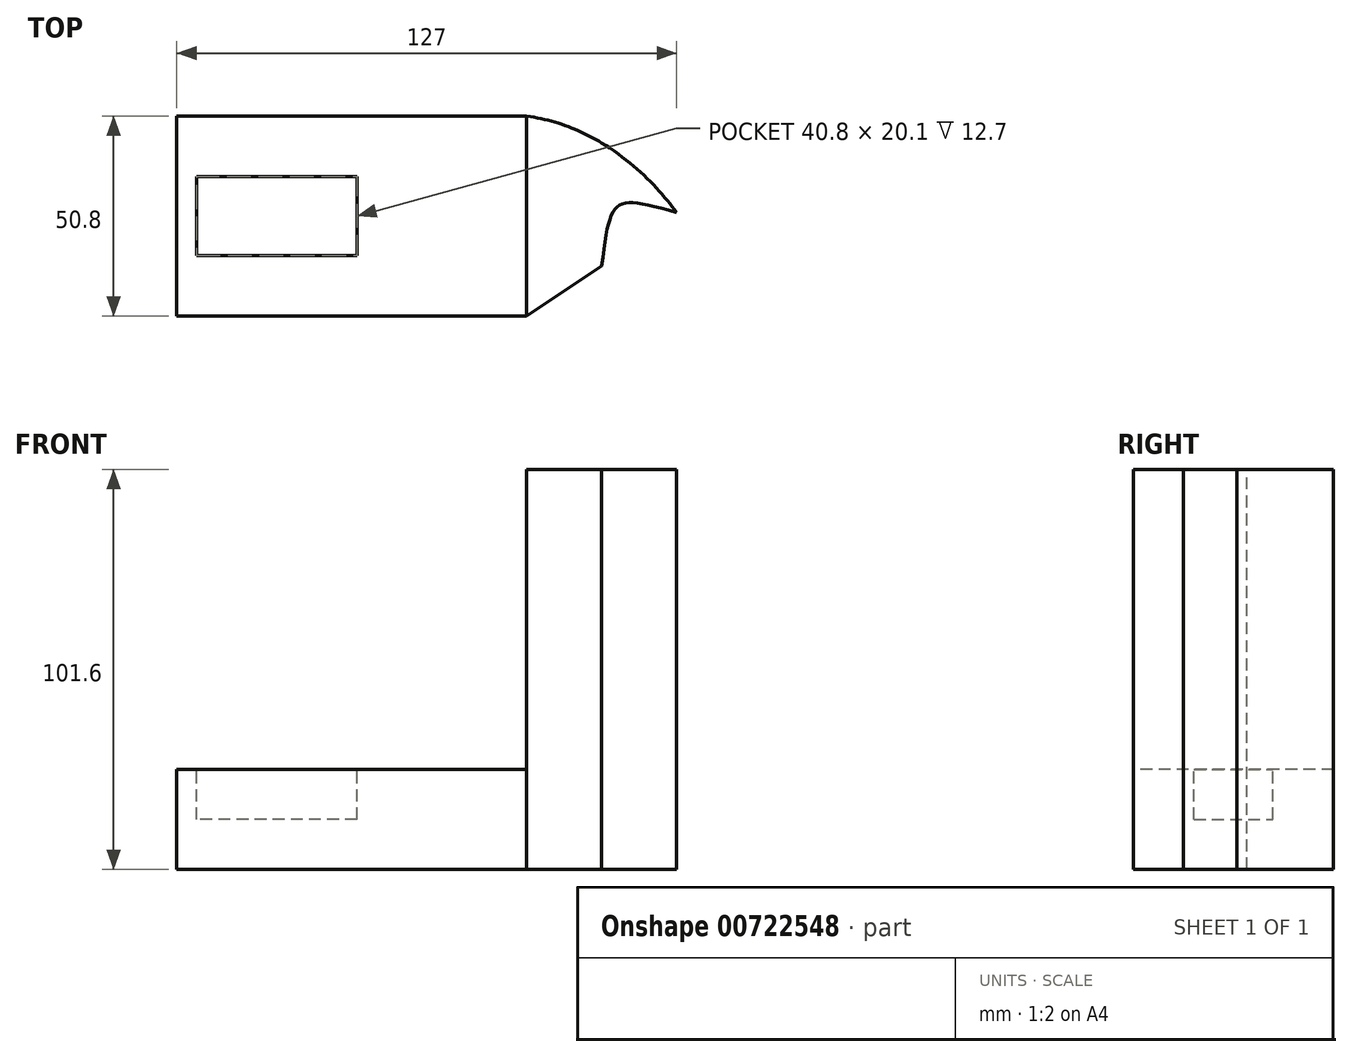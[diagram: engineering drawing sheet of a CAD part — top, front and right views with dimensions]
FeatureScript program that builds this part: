
annotation { "Feature Type Name" : "Feature", "Feature Type Description" : "" }
export const myFeature = defineFeature(function(context is Context, id is Id, definition is map)
    precondition{}
    {
        {
            var Q0;
            Q0=qCreatedBy(makeId("Top.planeOp"),FACE);
            var sketch = newSketch(context, id + "F0", { "sketchPlane" : qUnion([Q0])});
            skLineSegment(sketch, "E0.bottom", {"start": v(50.8, -25.4) * mm, "end": v(-50.8, -25.4) * mm});
            skLineSegment(sketch, "E0.top", {"start": v(50.8, 25.4) * mm, "end": v(-50.8, 25.4) * mm});
            skLineSegment(sketch, "E0.left", {"start": v(50.8, -25.4) * mm, "end": v(50.8, 25.4) * mm});
            skLineSegment(sketch, "E0.right", {"start": v(-50.8, -25.4) * mm, "end": v(-50.8, 25.4) * mm});
            skPoint(sketch, "E0.middle", {"position": v(0, 0) * mm});
            skSolve(sketch);
        }
        {
            var Q0;
            Q0=makeQuery(id+"F0.imprint","IMPRINT",FACE,{"disambiguationData":[TD([[makeQuery(id+"F0.imprint","IMPRINT",EDGE,{"derivedFrom":sQuery(id+"F0.wireOp",EDGE,"E0.bottom")}),-1.0]])]});
            extrude(context, id + "F1", {"entities" : qUnion([Q0]), "depth" : 25.4 * mm, "offsetDistance" : 25.4 * mm});
        }
        {
            var Q0;
            Q0=makeQuery(id+"F1.opExtrude","CAP_FACE",FACE,{"disambiguationData":[OSD([sQuery(id+"F0.wireOp",EDGE,"E0.bottom"),sQuery(id+"F0.wireOp",EDGE,"E0.top"),sQuery(id+"F0.wireOp",EDGE,"E0.left"),sQuery(id+"F0.wireOp",EDGE,"E0.right")])],"isStart":false});
            var sketch = newSketch(context, id + "F2", { "sketchPlane" : qUnion([Q0])});
            skLineSegment(sketch, "E1", {"start": v(-50.8, 25.4) * mm, "end": v(0, -25.4) * mm});
            skLineSegment(sketch, "E2", {"start": v(0, -25.4) * mm, "end": v(0, 25.4) * mm});
            skLineSegment(sketch, "E3", {"start": v(0, 25.4) * mm, "end": v(-50.8, -25.4) * mm});
            skCircle(sketch, "E4", {"center": v(-25.4, 0) * mm, "radius": 14.63 * mm});
            skCircle(sketch, "E5", {"center": v(-25.4, 0) * mm, "radius": 3.81 * mm});
            skLineSegment(sketch, "E6.bottom", {"start": v(-5, -10.05) * mm, "end": v(-45.8, -10.05) * mm});
            skLineSegment(sketch, "E6.top", {"start": v(-5, 10.05) * mm, "end": v(-45.8, 10.05) * mm});
            skLineSegment(sketch, "E6.left", {"start": v(-5, -10.05) * mm, "end": v(-5, 10.05) * mm});
            skLineSegment(sketch, "E6.right", {"start": v(-45.8, -10.05) * mm, "end": v(-45.8, 10.05) * mm});
            skSolve(sketch);
        }
        {
            var Q0;
            {var subQ0=sQuery(id+"F2.wireOp",EDGE,"E3");var subQ1=sQuery(id+"F2.wireOp",EDGE,"E1");var subQ2=makeQuery(id+"F2.imprint","INTERSECT",VERTEX,{"derivedFrom":[subQ1,subQ0]});Q0=makeQuery(id+"F2.imprint","IMPRINT",FACE,{"disambiguationData":[TD([[makeQuery(id+"F2.imprint","IMPRINT",EDGE,{"disambiguationData":[TD([[subQ2,-1.0]])],"derivedFrom":subQ1}),1.0]])]});}
            var Q1;
            {var subQ0=sQuery(id+"F2.wireOp",EDGE,"E5");var subQ1=sQuery(id+"F2.wireOp",EDGE,"E1");var subQ2=makeQuery(id+"F2.imprint","INTERSECT",VERTEX,{"disambiguationData":[OD(0.0)],"derivedFrom":[subQ1,subQ0]});Q1=makeQuery(id+"F2.imprint","IMPRINT",FACE,{"disambiguationData":[TD([[makeQuery(id+"F2.imprint","IMPRINT",EDGE,{"disambiguationData":[TD([[subQ2,-1.0]])],"derivedFrom":subQ1}),1.0]])]});}
            var Q2;
            {var subQ0=sQuery(id+"F2.wireOp",EDGE,"E5");var subQ1=sQuery(id+"F2.wireOp",EDGE,"E1");var subQ2=makeQuery(id+"F2.imprint","INTERSECT",VERTEX,{"disambiguationData":[OD(0.0)],"derivedFrom":[subQ1,subQ0]});Q2=makeQuery(id+"F2.imprint","IMPRINT",FACE,{"disambiguationData":[TD([[makeQuery(id+"F2.imprint","IMPRINT",EDGE,{"disambiguationData":[TD([[subQ2,-1.0]])],"derivedFrom":subQ1}),-1.0]])]});}
            var Q3;
            {var subQ0=sQuery(id+"F2.wireOp",EDGE,"E3");var subQ1=sQuery(id+"F2.wireOp",EDGE,"E1");var subQ2=makeQuery(id+"F2.imprint","INTERSECT",VERTEX,{"derivedFrom":[subQ1,subQ0]});Q3=makeQuery(id+"F2.imprint","IMPRINT",FACE,{"disambiguationData":[TD([[makeQuery(id+"F2.imprint","IMPRINT",EDGE,{"disambiguationData":[TD([[subQ2,-1.0]])],"derivedFrom":subQ1}),-1.0]])]});}
            var Q4;
            {var subQ5=sQuery(id+"F2.wireOp",EDGE,"E6.left");Q4=makeQuery(id+"F2.imprint","IMPRINT",FACE,{"disambiguationData":[TD([[makeQuery(id+"F2.imprint","IMPRINT",EDGE,{"derivedFrom":subQ5}),1.0]])]});}
            var Q5;
            {var subQ0=sQuery(id+"F2.wireOp",EDGE,"E6.top");var subQ1=sQuery(id+"F2.wireOp",EDGE,"E1");var subQ2=makeQuery(id+"F2.imprint","INTERSECT",VERTEX,{"derivedFrom":[subQ1,subQ0]});Q5=makeQuery(id+"F2.imprint","IMPRINT",FACE,{"disambiguationData":[TD([[makeQuery(id+"F2.imprint","IMPRINT",EDGE,{"disambiguationData":[TD([[subQ2,-1.0]])],"derivedFrom":subQ1}),1.0]])]});}
            var Q6;
            {var subQ0=sQuery(id+"F2.wireOp",EDGE,"E5");var subQ1=sQuery(id+"F2.wireOp",EDGE,"E1");var subQ2=makeQuery(id+"F2.imprint","INTERSECT",VERTEX,{"disambiguationData":[OD(1.0)],"derivedFrom":[subQ1,subQ0]});Q6=makeQuery(id+"F2.imprint","IMPRINT",FACE,{"disambiguationData":[TD([[makeQuery(id+"F2.imprint","IMPRINT",EDGE,{"disambiguationData":[TD([[subQ2,-1.0]])],"derivedFrom":subQ1}),-1.0]])]});}
            var Q7;
            {var subQ5=sQuery(id+"F2.wireOp",EDGE,"E6.right");Q7=makeQuery(id+"F2.imprint","IMPRINT",FACE,{"disambiguationData":[TD([[makeQuery(id+"F2.imprint","IMPRINT",EDGE,{"derivedFrom":subQ5}),-1.0]])]});}
            var Q8;
            {var subQ0=sQuery(id+"F2.wireOp",EDGE,"E5");var subQ1=sQuery(id+"F2.wireOp",EDGE,"E1");var subQ2=makeQuery(id+"F2.imprint","INTERSECT",VERTEX,{"disambiguationData":[OD(1.0)],"derivedFrom":[subQ1,subQ0]});Q8=makeQuery(id+"F2.imprint","IMPRINT",FACE,{"disambiguationData":[TD([[makeQuery(id+"F2.imprint","IMPRINT",EDGE,{"disambiguationData":[TD([[subQ2,-1.0]])],"derivedFrom":subQ1}),1.0]])]});}
            var Q9;
            {var subQ1=sQuery(id+"F2.wireOp",EDGE,"E1");var subQ5=sQuery(id+"F2.wireOp",EDGE,"E6.top");var subQ6=makeQuery(id+"F2.imprint","INTERSECT",VERTEX,{"derivedFrom":[subQ1,subQ5]});Q9=makeQuery(id+"F2.imprint","IMPRINT",FACE,{"disambiguationData":[TD([[makeQuery(id+"F2.imprint","IMPRINT",EDGE,{"disambiguationData":[TD([[subQ6,-1.0]])],"derivedFrom":subQ1}),-1.0]])]});}
            extrude(context, id + "F3", {"entities" : qUnion([Q0, Q1, Q2, Q3, Q4, Q5, Q6, Q7, Q8, Q9]), "operationType" : NewBodyOperationType.REMOVE, "oppositeDirection" : true, "depth" : 12.7 * mm, "offsetDistance" : 25.4 * mm});
        }
        {
            var Q0;
            Q0=makeQuery(id+"F1.opExtrude","CAP_FACE",FACE,{"disambiguationData":[OSD([sQuery(id+"F0.wireOp",EDGE,"E0.bottom"),sQuery(id+"F0.wireOp",EDGE,"E0.top"),sQuery(id+"F0.wireOp",EDGE,"E0.left"),sQuery(id+"F0.wireOp",EDGE,"E0.right")])],"isStart":false});
            var sketch = newSketch(context, id + "F4", { "sketchPlane" : qUnion([Q0])});
            skLineSegment(sketch, "E7.bottom", {"start": v(50.8, 25.4) * mm, "end": v(38.1, 25.4) * mm});
            skLineSegment(sketch, "E7.top", {"start": v(50.8, -25.4) * mm, "end": v(38.1, -25.4) * mm});
            skLineSegment(sketch, "E7.left", {"start": v(50.8, 25.4) * mm, "end": v(50.8, -25.4) * mm});
            skLineSegment(sketch, "E7.right", {"start": v(38.1, 25.4) * mm, "end": v(38.1, -25.4) * mm});
            skSolve(sketch);
        }
        {
            var Q0;
            Q0=makeQuery(id+"F4.imprint","IMPRINT",FACE,{"disambiguationData":[TD([[makeQuery(id+"F4.imprint","IMPRINT",EDGE,{"derivedFrom":sQuery(id+"F4.wireOp",EDGE,"E7.bottom")}),1.0]])]});
            extrude(context, id + "F5", {"entities" : qUnion([Q0]), "operationType" : NewBodyOperationType.ADD, "depth" : 76.2 * mm, "offsetDistance" : 25.4 * mm});
        }
        {
            var Q0;
            Q0=makeQuery(id+"F5.boolean.opBoolean","MERGE",FACE,{"derivedFrom":[makeQuery(id+"F1.opExtrude","SWEPT_FACE",FACE,{"disambiguationData":[OSD([sQuery(id+"F0.wireOp",EDGE,"E0.left")])]}),makeQuery(id+"F5.opExtrude","SWEPT_FACE",FACE,{"disambiguationData":[OSD([sQuery(id+"F4.wireOp",EDGE,"E7.left")])]})]});
            extrude(context, id + "F6", {"entities" : qUnion([Q0]), "operationType" : NewBodyOperationType.ADD, "depth" : 25.4 * mm, "offsetDistance" : 25.4 * mm});
        }
        {
            var Q0;
            {var subQ0=sQuery(id+"F4.wireOp",EDGE,"E7.left");Q0=makeQuery(id+"F6.boolean.opBoolean","MERGE",FACE,{"derivedFrom":[makeQuery(id+"F5.opExtrude","CAP_FACE",FACE,{"disambiguationData":[OSD([sQuery(id+"F4.wireOp",EDGE,"E7.bottom"),sQuery(id+"F4.wireOp",EDGE,"E7.top"),subQ0,sQuery(id+"F4.wireOp",EDGE,"E7.right")])],"isStart":false}),makeQuery(id+"F6.opExtrude","SWEPT_FACE",FACE,{"disambiguationData":[OSD([subQ0])]})]});}
            var sketch = newSketch(context, id + "F7", { "sketchPlane" : qUnion([Q0])});
            skLineSegment(sketch, "E8", {"start": v(38.1, -25.4) * mm, "end": v(38.1, 25.4) * mm});
            skLineSegment(sketch, "E9", {"start": v(38.1, 25.4) * mm, "end": v(76.2, 25.4) * mm});
            skLineSegment(sketch, "E10", {"start": v(57.15, -25.4) * mm, "end": v(57.15, 25.4) * mm});
            skLineSegment(sketch, "E11", {"start": v(38.1, -25.4) * mm, "end": v(57.15, -12.76) * mm});
            skFitSpline(sketch, "E12", {"points": [v(38.1, 25.4) * mm, v(76.2, 0) * mm], "startDerivative": vector(114.98, -15.5) * mm, "endDerivative": vector(-44.78, 89.05) * mm});
            skSolve(sketch);
        }
        {
            var Q0;
            {var subQ1=sQuery(id+"F7.wireOp",EDGE,"E9");var subQ3=sQuery(id+"F7.wireOp",EDGE,"E10");var subQ4=makeQuery(id+"F7.imprint","INTERSECT",VERTEX,{"derivedFrom":[subQ1,subQ3]});Q0=makeQuery(id+"F7.imprint","IMPRINT",FACE,{"disambiguationData":[TD([[makeQuery(id+"F7.imprint","IMPRINT",EDGE,{"disambiguationData":[TD([[subQ4,1.0]])],"derivedFrom":subQ3}),1.0]])]});}
            var Q1;
            {var subQ0=sQuery(id+"F7.wireOp",EDGE,"E9");var subQ1=makeQuery(id+"F6.opExtrude","CAP_EDGE",EDGE,{"disambiguationData":[OSD([sQuery(id+"F4.wireOp",EDGE,"E7.left")])],"isStart":false});var subQ2=makeQuery(id+"F7.imprint","INTERSECT",VERTEX,{"derivedFrom":[subQ1,subQ0]});Q1=makeQuery(id+"F7.imprint","IMPRINT",FACE,{"disambiguationData":[TD([[makeQuery(id+"F7.imprint","IMPRINT",EDGE,{"disambiguationData":[TD([[subQ2,-1.0]])],"derivedFrom":subQ0}),1.0]])]});}
            extrude(context, id + "F8", {"entities" : qUnion([Q0, Q1]), "operationType" : NewBodyOperationType.REMOVE, "oppositeDirection" : true, "depth" : 228.6 * mm, "offsetDistance" : 25.4 * mm});
        }
        {
            var Q0;
            {var subQ0=sQuery(id+"F4.wireOp",EDGE,"E7.left");Q0=makeQuery(id+"F6.boolean.opBoolean","MERGE",FACE,{"derivedFrom":[makeQuery(id+"F5.opExtrude","CAP_FACE",FACE,{"disambiguationData":[OSD([sQuery(id+"F4.wireOp",EDGE,"E7.bottom"),sQuery(id+"F4.wireOp",EDGE,"E7.top"),subQ0,sQuery(id+"F4.wireOp",EDGE,"E7.right")])],"isStart":false}),makeQuery(id+"F6.opExtrude","SWEPT_FACE",FACE,{"disambiguationData":[OSD([subQ0])]})]});}
            var sketch = newSketch(context, id + "F9", { "sketchPlane" : qUnion([Q0])});
            skLineSegment(sketch, "E13", {"start": v(57.15, -25.4) * mm, "end": v(57.15, 18.58) * mm});
            skLineSegment(sketch, "E14", {"start": v(38.1, -25.4) * mm, "end": v(57.15, -12.76) * mm});
            skSolve(sketch);
        }
        {
            var Q0;
            Q0=qSketchRegion(id+"F9",true);
            var Q1;
            {var subQ4=sQuery(id+"F9.wireOp",EDGE,"E14");Q1=makeQuery(id+"F9.imprint","IMPRINT",FACE,{"disambiguationData":[TD([[makeQuery(id+"F9.imprint","IMPRINT",EDGE,{"derivedFrom":subQ4}),-1.0]])]});}
            extrude(context, id + "F10", {"entities" : qUnion([Q0, Q1]), "operationType" : NewBodyOperationType.REMOVE, "oppositeDirection" : true, "depth" : 228.6 * mm, "offsetDistance" : 25.4 * mm});
        }
        {
            var Q0;
            {var subQ0=sQuery(id+"F4.wireOp",EDGE,"E7.left");Q0=makeQuery(id+"F6.boolean.opBoolean","MERGE",FACE,{"derivedFrom":[makeQuery(id+"F5.opExtrude","CAP_FACE",FACE,{"disambiguationData":[OSD([sQuery(id+"F4.wireOp",EDGE,"E7.bottom"),sQuery(id+"F4.wireOp",EDGE,"E7.top"),subQ0,sQuery(id+"F4.wireOp",EDGE,"E7.right")])],"isStart":false}),makeQuery(id+"F6.opExtrude","SWEPT_FACE",FACE,{"disambiguationData":[OSD([subQ0])]})]});}
            var sketch = newSketch(context, id + "F11", { "sketchPlane" : qUnion([Q0])});
            skFitSpline(sketch, "E15", {"points": [v(57.15, -12.76) * mm, v(76.2, 0.91) * mm], "startDerivative": vector(7.22, 54.45) * mm, "endDerivative": vector(49.93, -13.42) * mm});
            skSolve(sketch);
        }
        {
            var Q0;
            Q0=makeQuery(id+"F11.imprint","IMPRINT",FACE,{"disambiguationData":[TD([[makeQuery(id+"F11.imprint","IMPRINT",EDGE,{"derivedFrom":sQuery(id+"F11.wireOp",EDGE,"E15")}),-1.0]])]});
            extrude(context, id + "F12", {"entities" : qUnion([Q0]), "operationType" : NewBodyOperationType.REMOVE, "oppositeDirection" : true, "depth" : 228.6 * mm, "offsetDistance" : 25.4 * mm});
        }
    });
